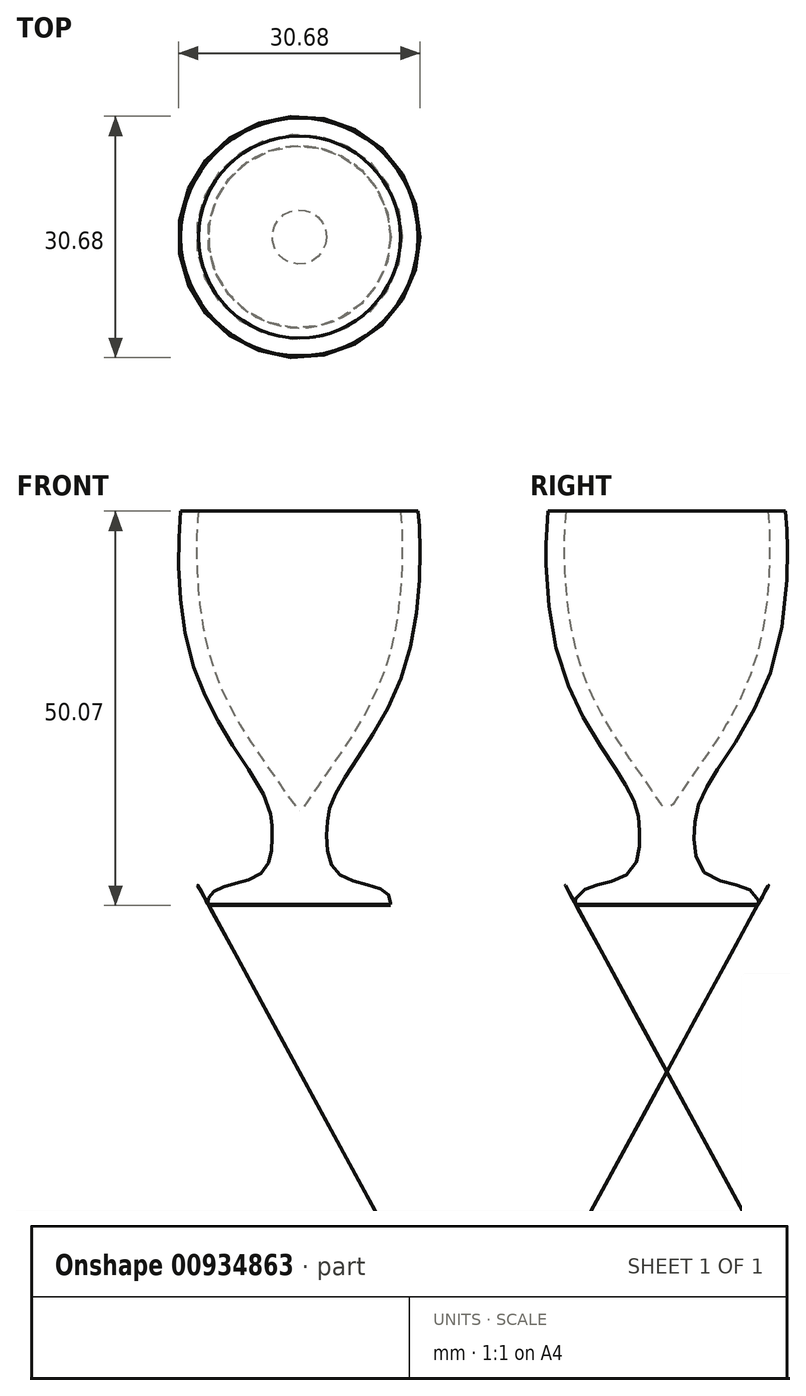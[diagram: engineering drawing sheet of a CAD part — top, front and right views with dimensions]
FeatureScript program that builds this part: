
annotation { "Feature Type Name" : "Feature", "Feature Type Description" : "" }
export const myFeature = defineFeature(function(context is Context, id is Id, definition is map)
    precondition{}
    {
        {
            var Q0;
            Q0=qCreatedBy(makeId("Front.planeOp"),FACE);
            var sketch = newSketch(context, id + "F0", { "sketchPlane" : qUnion([Q0])});
            skFitSpline(sketch, "E0", {"points": [v(15.09, 42.4) * mm, v(13.64, 23.34) * mm, v(4.71, 6.73) * mm, v(3.47, 1.86) * mm, v(4.54, -3.29) * mm, v(9.17, -5.18) * mm, v(11.55, -6.73) * mm, v(11.55, -7.67) * mm, v(11.55, -7.56) * mm], "startDerivative": vector(3.8, -30.76) * mm, "endDerivative": vector(0.44, 7.07) * mm});
            skLineSegment(sketch, "E1", {"start": v(11.55, -7.56) * mm, "end": v(0, -7.56) * mm});
            skLineSegment(sketch, "E2", {"start": v(15.09, 42.4) * mm, "end": v(12.82, 42.4) * mm});
            skFitSpline(sketch, "E3", {"points": [v(12.82, 42.4) * mm, v(11.33, 23.77) * mm, v(2.76, 8.1) * mm, v(0, 4.35) * mm], "startDerivative": vector(2.84, -19.87) * mm, "endDerivative": vector(-12.01, -9.46) * mm});
            skLineSegment(sketch, "E4", {"start": v(0, 4.35) * mm, "end": v(0, -7.56) * mm});
            skSolve(sketch);
        }
        {
            var Q0;
            Q0=makeQuery(id+"F0.imprint","IMPRINT",FACE,{"disambiguationData":[TD([[makeQuery(id+"F0.imprint","IMPRINT",EDGE,{"derivedFrom":sQuery(id+"F0.wireOp",EDGE,"E0")}),-1.0]])]});
            var Q1;
            Q1=sQuery(id+"F0.wireOp",EDGE,"E4");
            revolve(context, id + "F1", {"surfaceOperationType" : NewSurfaceOperationType.NEW, "entities" : qUnion([Q0]), "axis" : qUnion([Q1]), "revolveType" : RevolveType.FULL});
        }
        {
            var Q0;
            Q0=qCreatedBy(makeId("Front.planeOp"),FACE);
            var sketch = newSketch(context, id + "F2", { "sketchPlane" : qUnion([Q0])});
            skFitSpline(sketch, "E5", {"points": [v(15.28, 37.77) * mm, v(20.9, 29.26) * mm, v(15.21, 16.97) * mm, v(8.46, 12.34) * mm], "startDerivative": vector(55.64, -5.12) * mm, "endDerivative": vector(-38.47, 2.2) * mm});
            skSolve(sketch);
        }
        {
            var Q0;
            Q0=qCreatedBy(makeId("Right.planeOp"),FACE);
            cPlane(context, id + "F3", {"entities" : qUnion([Q0]), "cplaneType" : CPlaneType.OFFSET, "offset" : 16 * mm, "width" : 150 * mm, "height" : 150 * mm});
        }
        {
            var Q0;
            Q0=qCreatedBy(id+"F3.planeOp",FACE);
            var sketch = newSketch(context, id + "F4", { "sketchPlane" : qUnion([Q0])});
            skPoint(sketch, "E6.0", {"position": v(0, 37.77) * mm});
            skEllipse(sketch, "E7", {"center": v(0, 37.77) * mm, "majorRadius": 1.5 * mm, "minorRadius": 1.5 * mm, "majorAxis": v(0, 1)});
            skSolve(sketch);
        }
    });
